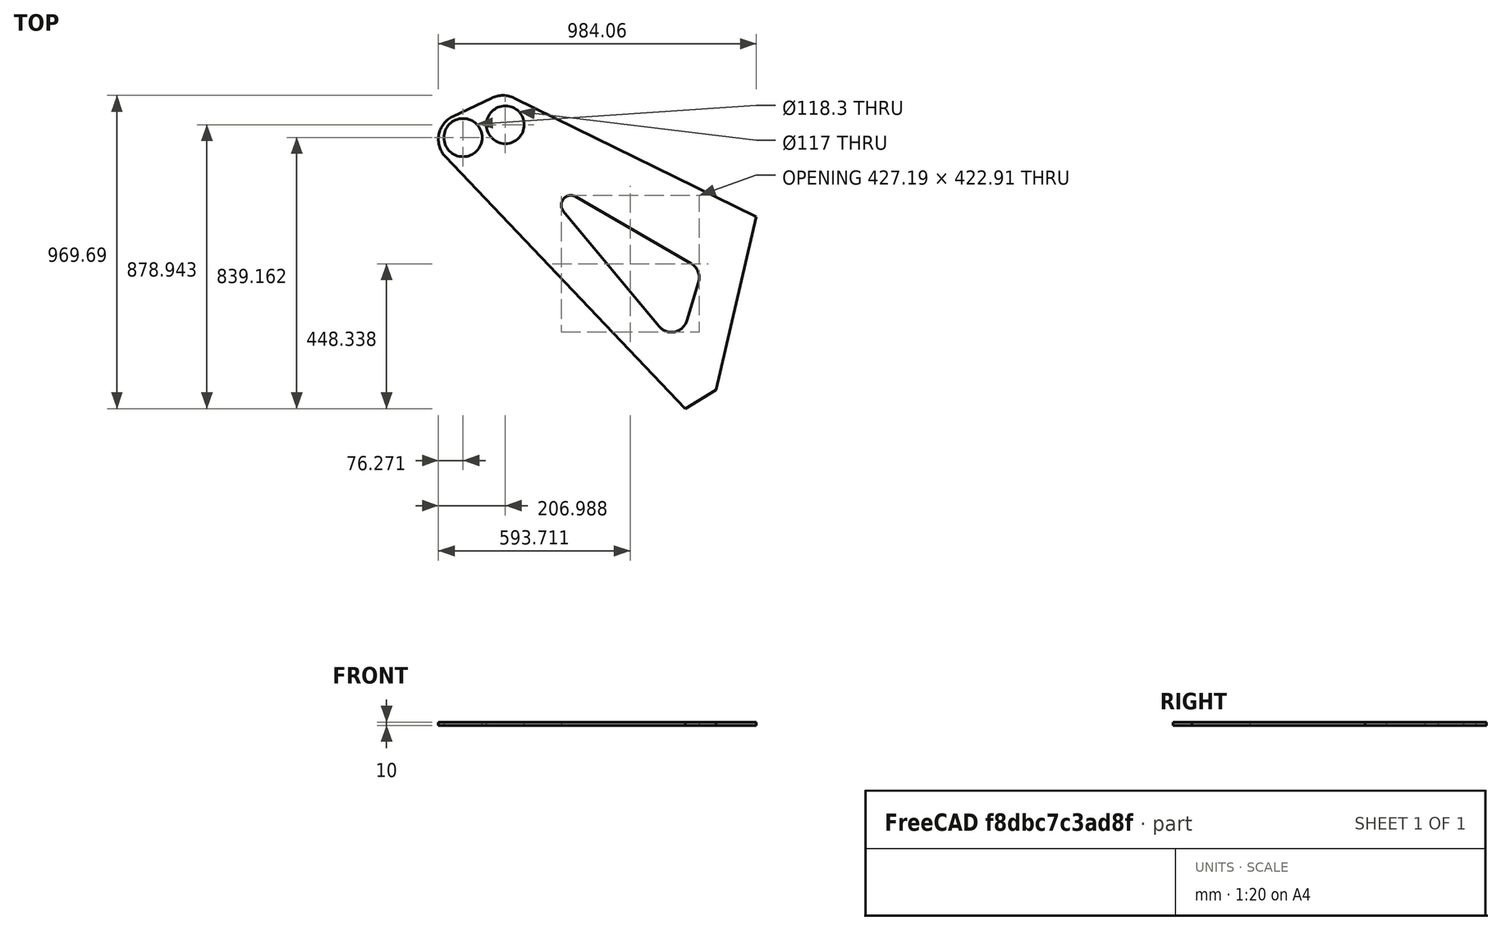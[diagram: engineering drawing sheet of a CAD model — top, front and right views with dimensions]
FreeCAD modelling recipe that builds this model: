
FCSTD DOCUMENT  (FreeCAD 1.0R39319 (Git))
Label: comp25_16mm_plate
License: All rights reserved
LicenseURL: https://en.wikipedia.org/wiki/All_rights_reserved
objects: Sketcher::SketchObject×1, PartDesign::Pad×1, PartDesign::Body×1
note: 6 computed .brp shape members not serialized (recipe doc carries the construction recipe); baked Part::Feature solids carry a one-line shape summary decoded from their .brp

FEATURE [Sketcher::SketchObject] Sketch
  ArcFitTolerance = 1e-06
  AttachmentSupport = -> [XY_Plane]
  FullyConstrained = true
  MakeInternals = false
  MapMode = 5
  sketch-geometry (15):
    g0: LineSegment StartX=-424.386 StartY=871.427 StartZ=0 EndX=318.446 EndY=91.1227 EndZ=0
    g1: LineSegment StartX=318.446 StartY=91.1227 StartZ=0 EndX=413.307 EndY=149.46 EndZ=0
    g2: LineSegment StartX=413.307 StartY=149.46 StartZ=0 EndX=538.173 EndY=685.494 EndZ=0
    g3: LineSegment StartX=538.173 StartY=685.494 StartZ=0 EndX=-210.641 EndY=1052.54 EndZ=0
    g4: ArcOfCircle CenterX=-246.292 CenterY=979.81 CenterZ=0 NormalX=0 NormalY=0 NormalZ=1 AngleXU=0 Radius=81 StartAngle=1.11504 EndAngle=2.01535
    g5: LineSegment StartX=-281.127 StartY=1052.94 StartZ=0 EndX=-401.436 EndY=995.627 EndZ=0
    g6: ArcOfCircle CenterX=-367.892 CenterY=925.208 CenterZ=0 NormalX=0 NormalY=0 NormalZ=1 AngleXU=0 Radius=78 StartAngle=2.01535 EndAngle=3.90239
    g7: Circle CenterX=-238.902 CenterY=970.063 CenterZ=0 NormalX=0 NormalY=0 NormalZ=1 AngleXU=0 Radius=58.5
    g8: Circle CenterX=-369.619 CenterY=930.282 CenterZ=0 NormalX=0 NormalY=0 NormalZ=1 AngleXU=0 Radius=59.15
    g9: ArcOfCircle CenterX=-35.7749 CenterY=721.356 CenterZ=0 NormalX=0 NormalY=0 NormalZ=1 AngleXU=0 Radius=30 StartAngle=1.04542 EndAngle=3.83435
    g10: ArcOfCircle CenterX=275.294 CenterY=377.878 CenterZ=0 NormalX=0 NormalY=0 NormalZ=1 AngleXU=0 Radius=50 StartAngle=3.83435 EndAngle=5.98831
    g11: ArcOfCircle CenterX=311.456 CenterY=496.939 CenterZ=0 NormalX=0 NormalY=0 NormalZ=1 AngleXU=0 Radius=50 StartAngle=5.98831 EndAngle=7.3286
    g12: LineSegment StartX=-58.8596 StartY=702.196 StartZ=0 EndX=236.82 EndY=345.945 EndZ=0
    g13: LineSegment StartX=323.136 StartY=363.347 StartZ=0 EndX=359.298 EndY=482.408 EndZ=0
    g14: LineSegment StartX=-20.7287 StartY=747.31 StartZ=0 EndX=336.533 EndY=540.196 EndZ=0
  constraints (36):
    c: Coincident(g0,g1)
    c: Coincident(g1,g2)
    c: Coincident(g2,g3)
    c: Tangent(g3,g4) = -1.5708
    c: Tangent(g5,g6) = -1.5708
    c: Distance(g0,g0) = 1077.35
    c: Distance(g1,g1) = 111.364
    c: Distance(g2,g2) = 550.385
    c: Distance(g3,g3) = 833.935
    c: Distance(g5,g5) = 133.262
    c: Radius(g4) = 81
    c: Radius(g6) = 78
    c: Tangent(g4,g5) = -1.5708
    c: Diameter(g7) = 117
    c: DistanceX(g4,g7) = 7.3905
    c: Diameter(g8) = 118.3
    c: Distance(g6,g8) = 5.3592
    c: Tangent(g6,g0) = -1.5708
    c: Angle(g1,g0) = 1.78024
    c: Angle(g3,g2) = 1.79769
    c: Distance(g12,g12) = 462.97
    c: Diameter(g10) = 100
    c: Diameter(g11) = 100
    c: Diameter(g9) = 60
    c: Distance(g14,g14) = 412.955
    c: Distance(g13,g13) = 124.432
    c: Tangent(g9,g12) = -1.5708
    c: Tangent(g9,g14) = 1.5708
    c: Tangent(g10,g13) = -1.5708
    c: Tangent(g10,g12) = -1.5708
    c: Tangent(g11,g14) = 1.5708
    c: Tangent(g11,g13) = -1.5708
    c: Block(g14)
    c: Block(g7)
    c: Block(g8)
    c: Block(g0)
FEATURE [PartDesign::Pad] Pad
  Direction = (0,0,1)
  Length = 10
  Length2 = 10
  Profile = -> Sketch
  ReferenceAxis = -> Sketch [N_Axis]
  Refine = true
  Suppressed = false
  Type = 0
FEATURE [PartDesign::Body] Body
  AllowCompound = false
  Group = -> [Sketch,Pad]
  Origin = -> Origin
  Tip = -> Pad
